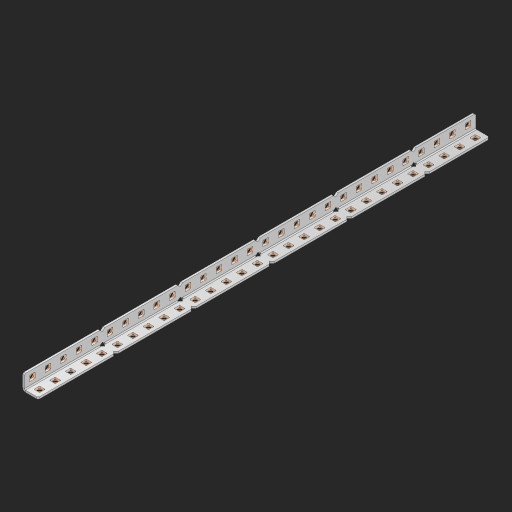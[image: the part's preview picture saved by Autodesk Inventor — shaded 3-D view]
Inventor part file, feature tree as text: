
AUTODESK INVENTOR PART (.ipt)
format: ipt  version: 2023 (Build 270158000, 158)  size: 1,001,472 bytes
history: native  units: in
note: dims shown in document units (in); Inventor stores cm internally (conversion verified against a paired STEP export)
features: other x64, extrude x59, sheet_metal_op x8, sketch x5, pattern_linear x1, mirror x1, chamfer x1
ambient origin geometry x8: Origin, YZ Plane, XZ Plane, XY Plane, X Axis, Y Axis, Z Axis, Center Point
bodies: Solid1 (feature_tree), Body (feature_tree)
feature tree (139):
  sheet_metal_op  "Flanges"
  sheet_metal_op  "Body Pattern"
  other  "Arc Length"
  pattern_linear  "Notch Pattern"  Spacing1=0.125in  [1 undecoded]
  other  "Diagonal Plane"
  mirror  "Everything Mirrored"
  chamfer  "End Chamfer"
  sketch  "Sketch1"  dims[d0=0.5in]
  other  "Plate1"
  sketch  "Sketch2"  dims[d1=14.5in]
  other  "Plate2"
  sheet_metal_op  "Bend1"
  sheet_metal_op  "Corner1"
  sketch  "Sketch8"  dims[d2=0.0625in]
  sketch  "Sketch9"  dims[d3=0.0625in]
  other  "Srf91"
  sheet_metal_op  "Body Pattern Sketch"
  other  "Srf92"
  sketch  "Sketch13"  dims[d4=0.0312in d5=0.125in d6=0.0625in d7=0.5in d8=90.0deg d9=0.0312in d10=0.25in d11=0.0625in d12=0.0625in d49=0.182in d50=0.02in d52=0.25in d53=0.0625in d54=0.0in d55=0.172in d56=1.0in d57=0.0in d85=0.1473in d86=0.1782in d89=0.0625in d90=0.0in d91=0.04in d92=0.0491in d95=2.5in d96=0.04in d97=0.25in d98=45.0deg d123=0.204in d126=0.0491in d127=0.1473in d128=0.08in d129=0.04in d130=2.5in d131=11.4173in d133=0.5in d134=0.3937in d136=1.0in]
  other  "Srf856"
  other  "Srf857"
  other  "Srf858"
  other  "Srf859"
  other  "Srf860"
  other  "Srf861"
  other  "Srf1275"
  other  "Srf1276"
  other  "Srf1278"
  other  "Srf1279"
  other  "Srf1280"
  other  "Srf1281"
  other  "Srf1282"
  other  "Srf1283"
  other  "Srf1383"
  other  "Srf1384"
  other  "Srf1385"
  other  "Srf1386"
  other  "Srf1387"
  other  "Srf1388"
  other  "Srf1389"
  other  "Srf1390"
  other  "Srf1391"
  other  "Srf1392"
  other  "Srf1393"
  other  "Srf1394"
  other  "Srf1395"
  other  "Srf1396"
  other  "Srf1397"
  other  "Srf1398"
  other  "Srf1399"
  other  "Srf1400"
  other  "Srf1401"
  other  "Srf1402"
  other  "Srf1403"
  other  "Srf1404"
  other  "Srf1475"
  other  "Srf1476"
  other  "Srf1477"
  other  "Srf1478"
  other  "Srf1479"
  other  "Srf1480"
  other  "Srf1481"
  other  "Srf1482"
  other  "Srf1483"
  other  "Srf1484"
  other  "Srf1485"
  other  "Srf1486"
  other  "Srf1487"
  other  "Srf1488"
  other  "Srf1489"
  other  "Srf1490"
  other  "Srf1491"
  other  "Srf1492"
  other  "Srf1493"
  other  "Srf1494"
  other  "Srf1495"
  other  "Srf1496"
  sheet_metal_op  "Body Stamp"
  sheet_metal_op  "Body Circle"
  sheet_metal_op  "Notch"
  extrude  "ExtrusionSrf92"  Depth=0.0625in
  extrude  "ExtrusionSrf856"  Depth=0.5in TaperAngle=90.0deg
  extrude  "ExtrusionSrf857"  Depth=0.25in
  extrude  "ExtrusionSrf858"  Depth=0.0625in
  extrude  "ExtrusionSrf859"  Depth=0.0625in
  extrude  "ExtrusionSrf860"  Depth=0.3937in
  extrude  "ExtrusionSrf861"  Depth=0.02in
  extrude  "ExtrusionSrf1275"  Depth=0.25in
  extrude  "ExtrusionSrf1276"  Depth=0.0625in
  extrude  "ExtrusionSrf1277"  TaperAngle=0.0deg  [1 undecoded]
  extrude  "ExtrusionSrf1278"  Depth=0.3937in
  extrude  "ExtrusionSrf1279"  Depth=0.3937in TaperAngle=0.0deg
  extrude  "ExtrusionSrf1280"  Depth=0.3937in
  extrude  "ExtrusionSrf1281"  Depth=0.3937in
  extrude  "ExtrusionSrf1282"  Depth=0.0625in
  extrude  "ExtrusionSrf1383"  Depth=0.3937in TaperAngle=0.0deg
  extrude  "ExtrusionSrf1384"  Depth=0.3937in
  extrude  "ExtrusionSrf1385"  Depth=0.25in TaperAngle=45.0deg
  extrude  "ExtrusionSrf1386"  Depth=0.3937in
  extrude  "ExtrusionSrf1387"  Depth=0.3937in
  extrude  "ExtrusionSrf1388"  Depth=0.3937in
  extrude  "ExtrusionSrf1389"  Depth=0.3937in
  extrude  "ExtrusionSrf1390"  Depth=0.3937in
  extrude  "ExtrusionSrf1391"  Depth=0.3937in
  extrude  "ExtrusionSrf1392"  Depth=0.3937in
  extrude  "ExtrusionSrf1393"  Depth=0.5in
  extrude  "ExtrusionSrf1394"  [1 undecoded]
  extrude  "ExtrusionSrf1395"  [1 undecoded]
  extrude  "ExtrusionSrf1396"  [1 undecoded]
  extrude  "ExtrusionSrf1397"  [1 undecoded]
  extrude  "ExtrusionSrf1398"  [1 undecoded]
  extrude  "ExtrusionSrf1399"  [1 undecoded]
  extrude  "ExtrusionSrf1400"  [1 undecoded]
  extrude  "ExtrusionSrf1401"  [1 undecoded]
  extrude  "ExtrusionSrf1402"  [1 undecoded]
  extrude  "ExtrusionSrf1403"  [1 undecoded]
  extrude  "ExtrusionSrf1404"  [1 undecoded]
  extrude  "ExtrusionSrf1475"  [1 undecoded]
  extrude  "ExtrusionSrf1476"  [1 undecoded]
  extrude  "ExtrusionSrf1477"  [1 undecoded]
  extrude  "ExtrusionSrf1478"  [1 undecoded]
  extrude  "ExtrusionSrf1479"  [1 undecoded]
  extrude  "ExtrusionSrf1480"  [1 undecoded]
  extrude  "ExtrusionSrf1481"  [1 undecoded]
  extrude  "ExtrusionSrf1482"  [1 undecoded]
  extrude  "ExtrusionSrf1483"  [1 undecoded]
  extrude  "ExtrusionSrf1484"  [1 undecoded]
  extrude  "ExtrusionSrf1485"  [1 undecoded]
  extrude  "ExtrusionSrf1486"  [1 undecoded]
  extrude  "ExtrusionSrf1487"  [1 undecoded]
  extrude  "ExtrusionSrf1488"  [1 undecoded]
  extrude  "ExtrusionSrf1489"  [1 undecoded]
  extrude  "ExtrusionSrf1490"  [1 undecoded]
  extrude  "ExtrusionSrf1491"  [1 undecoded]
  extrude  "ExtrusionSrf1492"  [1 undecoded]
  extrude  "ExtrusionSrf1493"  [1 undecoded]
  extrude  "ExtrusionSrf1494"  [1 undecoded]
  extrude  "ExtrusionSrf1495"  [1 undecoded]
  extrude  "ExtrusionSrf1496"  [1 undecoded]
note: 35 required parameter values undecoded (feature->parameter linkage not recoverable at this tier; creation-order binding heuristic only, values carry confidence <= 0.55)
